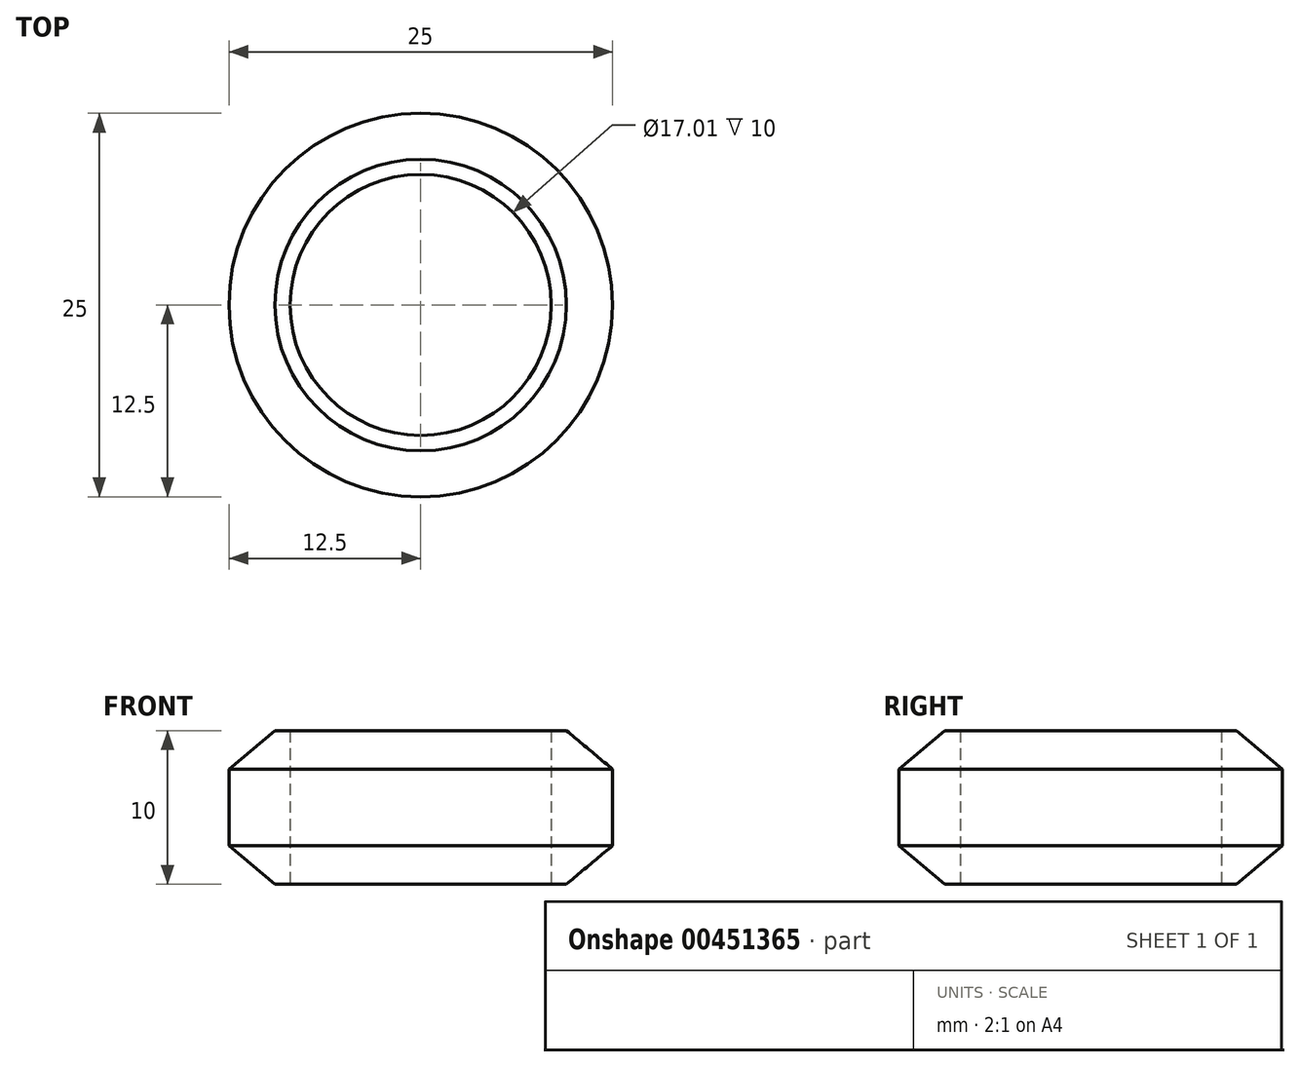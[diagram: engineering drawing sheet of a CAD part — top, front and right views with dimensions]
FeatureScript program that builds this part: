
annotation { "Feature Type Name" : "Feature", "Feature Type Description" : "" }
export const myFeature = defineFeature(function(context is Context, id is Id, definition is map)
    precondition{}
    {
        {
            var Q0;
            Q0=qCreatedBy(makeId("Top.planeOp"),FACE);
            var sketch = newSketch(context, id + "F0", { "sketchPlane" : qUnion([Q0])});
            skCircle(sketch, "E0", {"center": v(0, 0) * mm, "radius": 12.5 * mm});
            skSolve(sketch);
        }
        {
            var Q0;
            Q0=makeQuery(id+"F0.imprint","IMPRINT",FACE,{"disambiguationData":[TD([[makeQuery(id+"F0.imprint","IMPRINT",EDGE,{"derivedFrom":sQuery(id+"F0.wireOp",EDGE,"E0")}),1.0]])]});
            extrude(context, id + "F1", {"entities" : qUnion([Q0]), "depth" : 10 * mm});
        }
        {
            var Q0;
            Q0=qCreatedBy(makeId("Top.planeOp"),FACE);
            var sketch = newSketch(context, id + "F2", { "sketchPlane" : qUnion([Q0])});
            skCircle(sketch, "E1", {"center": v(0, 0) * mm, "radius": 8.5 * mm});
            skSolve(sketch);
        }
        {
            var Q0;
            Q0 = qSketchRegion(id + "F2", true);
            extrude(context, id + "F3", {"entities" : qUnion([Q0]), "operationType" : NewBodyOperationType.REMOVE, "depth" : 27.2 * mm});
        }
        {
            var Q0;
            Q0=makeQuery(id+"F1.opExtrude","SWEPT_FACE",FACE,{"disambiguationData":[OSD([sQuery(id+"F0.wireOp",EDGE,"E0")])]});
            chamfer(context, id + "F4", {"entities" : qUnion([Q0]), "chamferType" : ChamferType.TWO_OFFSETS, "width1" : 2.5 * mm, "oppositeDirection" : false, "width2" : 3 * mm, "tangentPropagation" : true});
        }
    });
